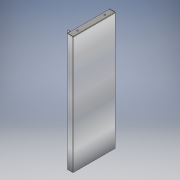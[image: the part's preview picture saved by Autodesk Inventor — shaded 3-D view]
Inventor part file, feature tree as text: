
AUTODESK INVENTOR PART (.ipt)
format: ipt  version: 2017 (Build 210142000, 142)  size: 332,800 bytes
history: native  units: mm
features: other x7, sketch x7, sheet_metal_op x6, extrude x4, reference x3, plane x1
ambient origin geometry x8: Origin, YZ Plane, XZ Plane, XY Plane, X Axis, Y Axis, Z Axis, Center Point
bodies: Solid1 (feature_tree)
feature tree (28):
  sheet_metal_op  "Contour Flange1"
  extrude  "Extrusion1"  Depth=40.0mm
  plane  "Work Plane1"
  other  "Decal1"
  extrude  "Extrusion2"  Depth=16.5mm
  extrude  "Extrusion3"  Depth=1.5mm
  sheet_metal_op  "Flange1"
  extrude  "Extrusion4"  Depth=1.5mm
  sketch  "Sketch1"  dims[d1=40.0mm d2=40.0mm]
  reference  "Reference1"
  reference  "Reference2"
  reference  "Reference3"
  other  "Plate1"
  sheet_metal_op  "Bend1"
  sheet_metal_op  "Corner1"
  sketch  "Sketch2"  dims[d3=22.0mm d4=16.5mm]
  sketch  "Sketch3"  dims[d5=1.5mm d6=0.75mm]
  other  "Image1"
  sketch  "Sketch4"  dims[d7=3.0mm d8=1.5mm]
  sketch  "Sketch5"  dims[d9=898.0mm]
  sketch  "Sketch6"  dims[d10=1.5mm]
  other  "Plate2"
  sheet_metal_op  "Bend2"
  sheet_metal_op  "Corner2"
  sketch  "Sketch7"  dims[d11=0.5mm d12=6.0mm d13=1.5mm d14=1.5mm d15=11.0mm d16=128.3mm d17=0.0mm d18=200.0mm d29=0.0mm d30=0.0mm d31=5.0mm d32=150.0mm d33=20.0mm d34=10.0mm d35=0.0mm d38=1.5mm d39=0.75mm d40=3.0mm d41=1.5mm d42=38.0mm d43=90.0deg d44=1.5mm d45=6.0mm d46=1.5mm d47=1.5mm d48=10.0mm d49=10.0mm d50=50.0mm d51=50.0mm d52=10.0mm d53=0.0mm]
  other  "Bancada de Lavagem Mãos - 1150 x 370 x 900h.iam"
  other  "Base:2"
  other  "Definition1"
